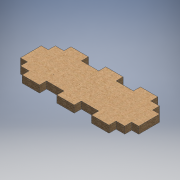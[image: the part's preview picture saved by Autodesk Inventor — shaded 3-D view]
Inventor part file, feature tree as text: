
AUTODESK INVENTOR PART (.ipt)
format: ipt  version: 2016 (Build 200138000, 138)  size: 173,568 bytes
history: native  units: mm
features: extrude x1, sketch x1
ambient origin geometry x8: Origin, YZ Plane, XZ Plane, XY Plane, X Axis, Y Axis, Z Axis, Center Point
bodies: Body1 (feature_tree)
feature tree (2):
  extrude  "Extrusion2"  Depth=15.766857mm
  sketch  "Sketch1"  dims[d0=6.39mm d1=15.766857mm d2=30.0mm d4=31.533715mm d5=10.0mm d8=10.0mm d10=18.958829mm d11=31.527659mm d12=94.601145mm d13=6.39mm d33=6.39mm d34=0.0mm]
